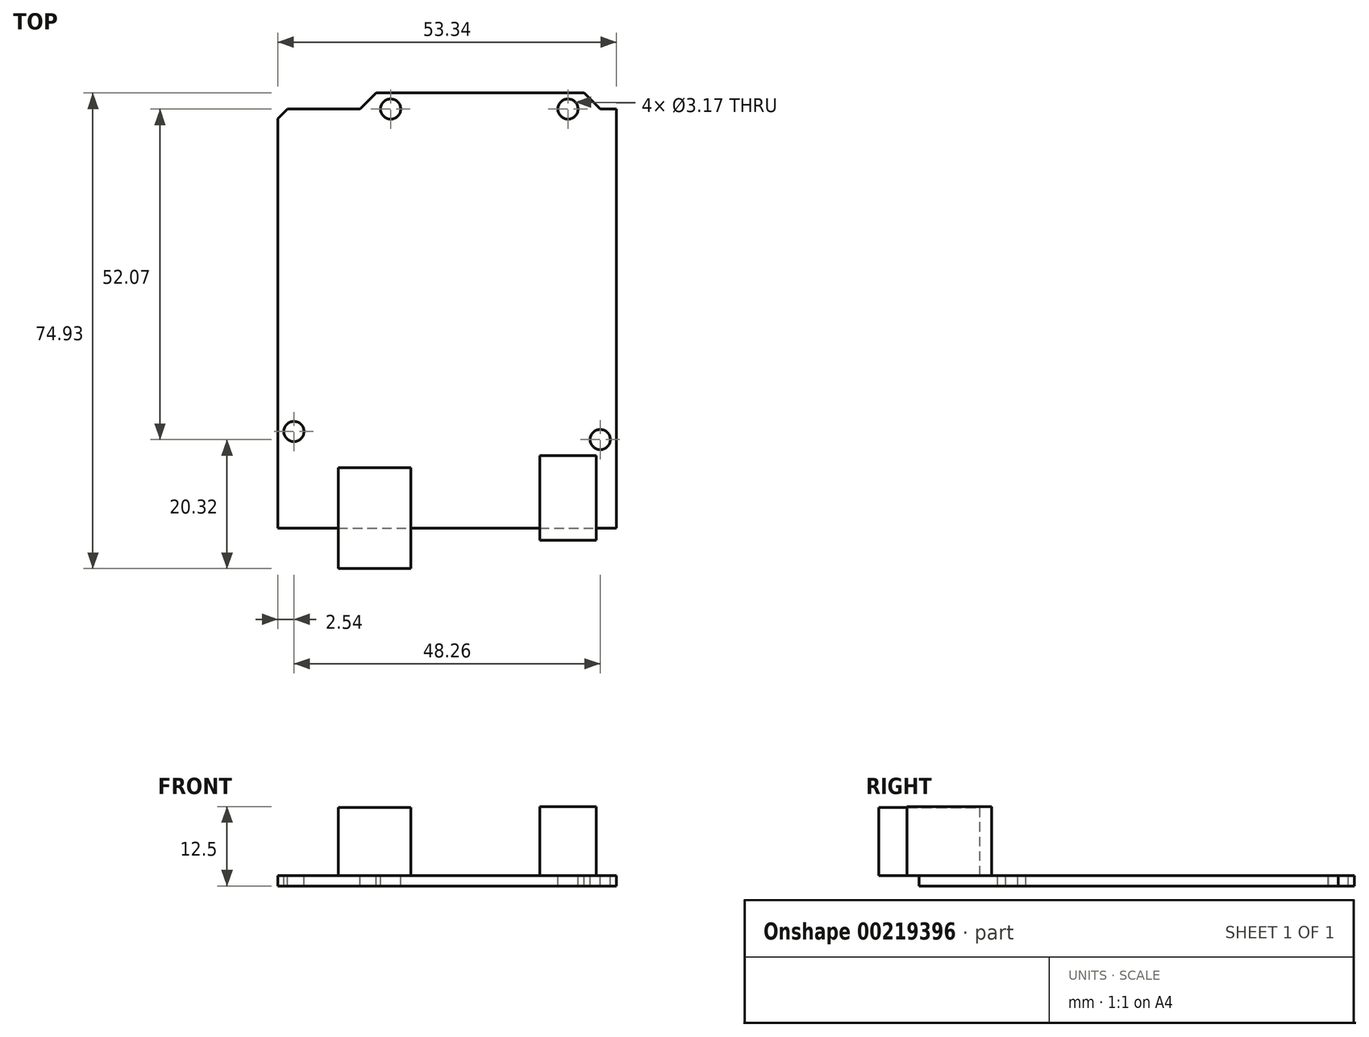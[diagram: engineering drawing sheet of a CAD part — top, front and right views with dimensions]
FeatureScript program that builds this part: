
annotation { "Feature Type Name" : "Feature", "Feature Type Description" : "" }
export const myFeature = defineFeature(function(context is Context, id is Id, definition is map)
    precondition{}
    {
        {
            var Q0;
            Q0=qCreatedBy(makeId("Top.planeOp"),FACE);
            var sketch = newSketch(context, id + "F0", { "sketchPlane" : qUnion([Q0])});
            skLineSegment(sketch, "E0", {"start": v(26.67, 0) * mm, "end": v(26.67, 66.04) * mm});
            skLineSegment(sketch, "E1", {"start": v(26.67, 66.04) * mm, "end": v(24.13, 66.04) * mm});
            skLineSegment(sketch, "E2", {"start": v(24.13, 66.04) * mm, "end": v(21.6, 68.58) * mm});
            skLineSegment(sketch, "E3", {"start": v(21.6, 68.58) * mm, "end": v(-11.18, 68.58) * mm});
            skLineSegment(sketch, "E4", {"start": v(-11.18, 68.58) * mm, "end": v(-13.72, 66.04) * mm});
            skLineSegment(sketch, "E5", {"start": v(-13.72, 66.04) * mm, "end": v(-25.15, 66.04) * mm});
            skLineSegment(sketch, "E6", {"start": v(-25.15, 66.04) * mm, "end": v(-26.67, 64.52) * mm});
            skLineSegment(sketch, "E7", {"start": v(-26.67, 64.52) * mm, "end": v(-26.67, 0) * mm});
            skLineSegment(sketch, "E8", {"start": v(-26.67, 0) * mm, "end": v(26.67, 0) * mm});
            skCircle(sketch, "E9", {"center": v(-24.13, 15.24) * mm, "radius": 1.59 * mm});
            skCircle(sketch, "E10", {"center": v(24.13, 13.97) * mm, "radius": 1.59 * mm});
            skCircle(sketch, "E11", {"center": v(-8.89, 66.04) * mm, "radius": 1.59 * mm});
            skCircle(sketch, "E12", {"center": v(19.05, 66.04) * mm, "radius": 1.59 * mm});
            skLineSegment(sketch, "E13.bottom", {"start": v(-17.14, -6.35) * mm, "end": v(-5.71, -6.35) * mm});
            skLineSegment(sketch, "E13.top", {"start": v(-17.14, 9.53) * mm, "end": v(-5.71, 9.53) * mm});
            skLineSegment(sketch, "E13.left", {"start": v(-17.14, -6.35) * mm, "end": v(-17.14, 9.53) * mm});
            skLineSegment(sketch, "E13.right", {"start": v(-5.71, -6.35) * mm, "end": v(-5.71, 9.53) * mm});
            skLineSegment(sketch, "E14.bottom", {"start": v(14.6, -1.9) * mm, "end": v(23.5, -1.9) * mm});
            skLineSegment(sketch, "E14.top", {"start": v(14.6, 11.43) * mm, "end": v(23.5, 11.43) * mm});
            skLineSegment(sketch, "E14.left", {"start": v(14.6, -1.9) * mm, "end": v(14.6, 11.43) * mm});
            skLineSegment(sketch, "E14.right", {"start": v(23.5, -1.9) * mm, "end": v(23.5, 11.43) * mm});
            skPoint(sketch, "E15", {"position": v(0, 0) * mm});
            skSolve(sketch);
        }
        {
            var Q0;
            {var subQ8=sQuery(id+"F0.wireOp",EDGE,"E0");Q0=makeQuery(id+"F0.imprint","IMPRINT",FACE,{"disambiguationData":[TD([[makeQuery(id+"F0.imprint","IMPRINT",EDGE,{"derivedFrom":subQ8}),1.0]])]});}
            var Q1;
            {var subQ5=sQuery(id+"F0.wireOp",EDGE,"E14.top");Q1=makeQuery(id+"F0.imprint","IMPRINT",FACE,{"disambiguationData":[TD([[makeQuery(id+"F0.imprint","IMPRINT",EDGE,{"derivedFrom":subQ5}),-1.0]])]});}
            var Q2;
            {var subQ5=sQuery(id+"F0.wireOp",EDGE,"E13.top");Q2=makeQuery(id+"F0.imprint","IMPRINT",FACE,{"disambiguationData":[TD([[makeQuery(id+"F0.imprint","IMPRINT",EDGE,{"derivedFrom":subQ5}),-1.0]])]});}
            var Q3;
            Q3=makeQuery(id+"F0.imprint","IMPRINT",FACE,{"disambiguationData":[TD([[makeQuery(id+"F0.imprint","IMPRINT",EDGE,{"derivedFrom":sQuery(id+"F0.wireOp",EDGE,"E9")}),-1.0]])]});
            var Q4;
            Q4=makeQuery(id+"F0.imprint","IMPRINT",FACE,{"disambiguationData":[TD([[makeQuery(id+"F0.imprint","IMPRINT",EDGE,{"derivedFrom":sQuery(id+"F0.wireOp",EDGE,"E11")}),-1.0]])]});
            var Q5;
            Q5=makeQuery(id+"F0.imprint","IMPRINT",FACE,{"disambiguationData":[TD([[makeQuery(id+"F0.imprint","IMPRINT",EDGE,{"derivedFrom":sQuery(id+"F0.wireOp",EDGE,"E12")}),-1.0]])]});
            var Q6;
            Q6=makeQuery(id+"F0.imprint","IMPRINT",FACE,{"disambiguationData":[TD([[makeQuery(id+"F0.imprint","IMPRINT",EDGE,{"derivedFrom":sQuery(id+"F0.wireOp",EDGE,"E10")}),-1.0]])]});
            extrude(context, id + "F1", {"entities" : qUnion([Q0, Q1, Q2, Q3, Q4, Q5, Q6]), "oppositeDirection" : true, "depth" : 1.6 * mm});
        }
        {
            var Q0;
            {var subQ5=sQuery(id+"F0.wireOp",EDGE,"E14.top");Q0=makeQuery(id+"F0.imprint","IMPRINT",FACE,{"disambiguationData":[TD([[makeQuery(id+"F0.imprint","IMPRINT",EDGE,{"derivedFrom":subQ5}),-1.0]])]});}
            var Q1;
            {var subQ5=sQuery(id+"F0.wireOp",EDGE,"E14.bottom");Q1=makeQuery(id+"F0.imprint","IMPRINT",FACE,{"disambiguationData":[TD([[makeQuery(id+"F0.imprint","IMPRINT",EDGE,{"derivedFrom":subQ5}),1.0]])]});}
            extrude(context, id + "F2", {"entities" : qUnion([Q0, Q1]), "operationType" : NewBodyOperationType.ADD, "depth" : 10.9 * mm});
        }
        {
            var Q0;
            {var subQ5=sQuery(id+"F0.wireOp",EDGE,"E13.top");Q0=makeQuery(id+"F0.imprint","IMPRINT",FACE,{"disambiguationData":[TD([[makeQuery(id+"F0.imprint","IMPRINT",EDGE,{"derivedFrom":subQ5}),-1.0]])]});}
            var Q1;
            {var subQ5=sQuery(id+"F0.wireOp",EDGE,"E13.bottom");Q1=makeQuery(id+"F0.imprint","IMPRINT",FACE,{"disambiguationData":[TD([[makeQuery(id+"F0.imprint","IMPRINT",EDGE,{"derivedFrom":subQ5}),1.0]])]});}
            extrude(context, id + "F3", {"entities" : qUnion([Q0, Q1]), "operationType" : NewBodyOperationType.ADD, "depth" : 10.75 * mm});
        }
    });
